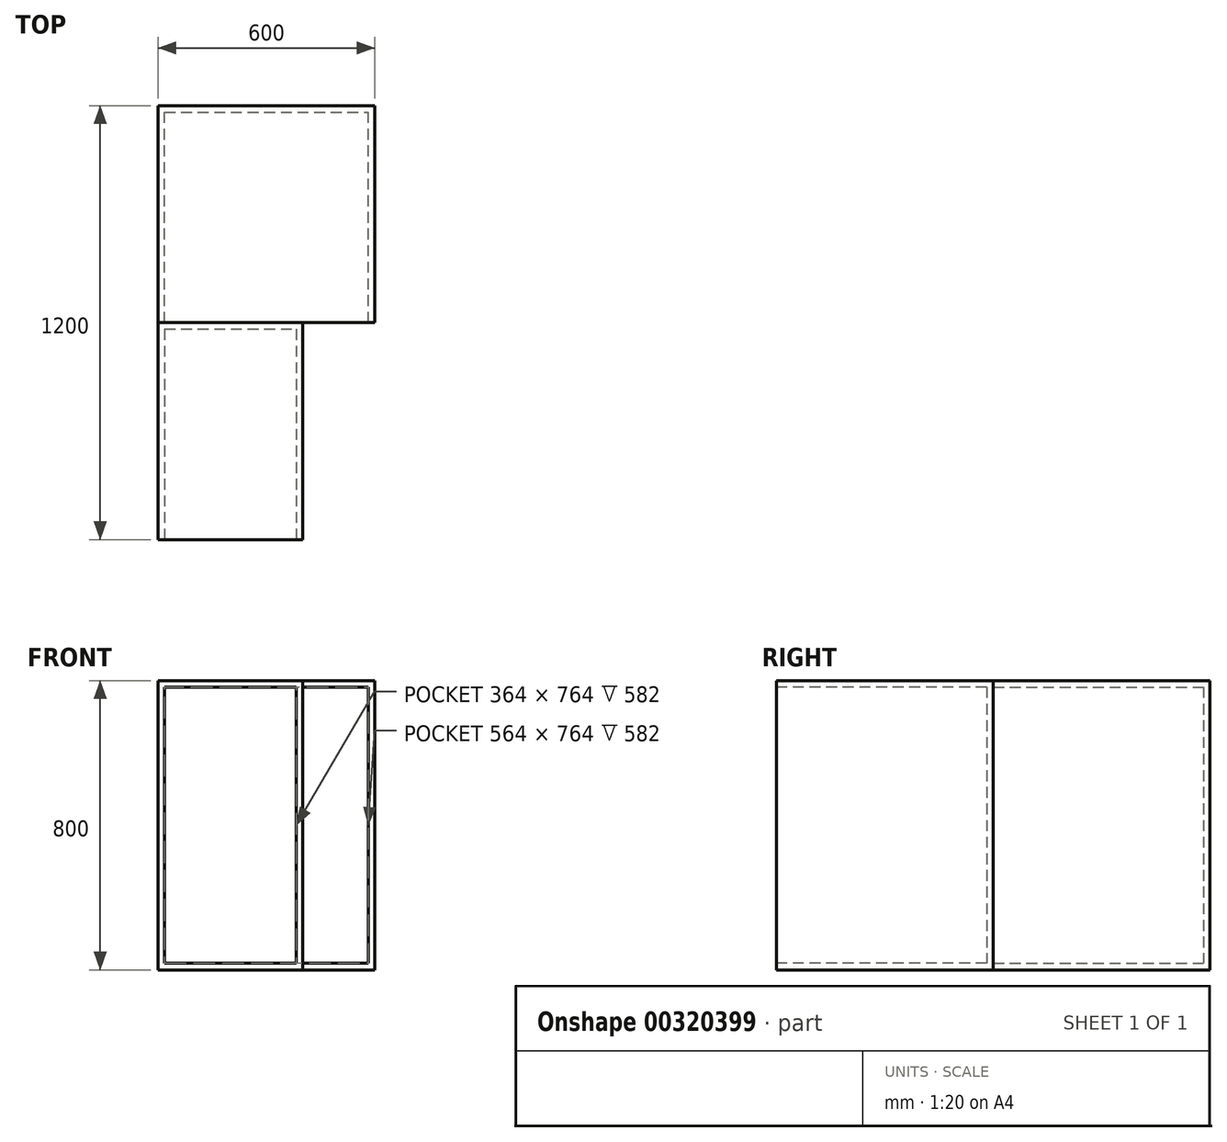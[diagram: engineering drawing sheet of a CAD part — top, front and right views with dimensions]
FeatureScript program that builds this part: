
annotation { "Feature Type Name" : "Feature", "Feature Type Description" : "" }
export const myFeature = defineFeature(function(context is Context, id is Id, definition is map)
    precondition{}
    {
        {
            var Q0;
            Q0=qCreatedBy(makeId("Top.planeOp"),FACE);
            var sketch = newSketch(context, id + "F0", { "sketchPlane" : qUnion([Q0])});
            skLineSegment(sketch, "E0.bottom", {"start": v(0, 0) * mm, "end": v(600, 0) * mm});
            skLineSegment(sketch, "E0.top", {"start": v(0, 600) * mm, "end": v(600, 600) * mm});
            skLineSegment(sketch, "E0.left", {"start": v(0, 0) * mm, "end": v(0, 600) * mm});
            skLineSegment(sketch, "E0.right", {"start": v(600, 0) * mm, "end": v(600, 600) * mm});
            skSolve(sketch);
        }
        {
            var Q0;
            Q0 = qSketchRegion(id + "F0", true);
            extrude(context, id + "F1", {"entities" : qUnion([Q0]), "depth" : 800 * mm});
        }
        {
            var Q0;
            Q0=qCreatedBy(makeId("Top.planeOp"),FACE);
            var sketch = newSketch(context, id + "F2", { "sketchPlane" : qUnion([Q0])});
            skLineSegment(sketch, "E1.bottom", {"start": v(0, 0) * mm, "end": v(400, 0) * mm});
            skLineSegment(sketch, "E1.top", {"start": v(0, -600) * mm, "end": v(400, -600) * mm});
            skLineSegment(sketch, "E1.left", {"start": v(0, 0) * mm, "end": v(0, -600) * mm});
            skLineSegment(sketch, "E1.right", {"start": v(400, 0) * mm, "end": v(400, -600) * mm});
            skSolve(sketch);
        }
        {
            var Q0;
            Q0=makeQuery(id+"F2.imprint","IMPRINT",FACE,{"disambiguationData":[TD([[makeQuery(id+"F2.imprint","IMPRINT",EDGE,{"derivedFrom":sQuery(id+"F2.wireOp",EDGE,"E1.bottom")}),-1.0]])]});
            extrude(context, id + "F3", {"entities" : qUnion([Q0]), "depth" : 800 * mm});
        }
        {
            var Q0;
            Q0=makeQuery(id+"F3.opExtrude","SWEPT_FACE",FACE,{"disambiguationData":[OSD([sQuery(id+"F2.wireOp",EDGE,"E1.top")])]});
            shell(context, id + "F4", {"entities" : qUnion([Q0]), "thickness" : 18 * mm});
        }
        {
            var Q0;
            Q0=makeQuery(id+"F1.opExtrude","SWEPT_FACE",FACE,{"disambiguationData":[OSD([sQuery(id+"F0.wireOp",EDGE,"E0.bottom")])]});
            shell(context, id + "F5", {"entities" : qUnion([Q0]), "thickness" : 18 * mm});
        }
    });
